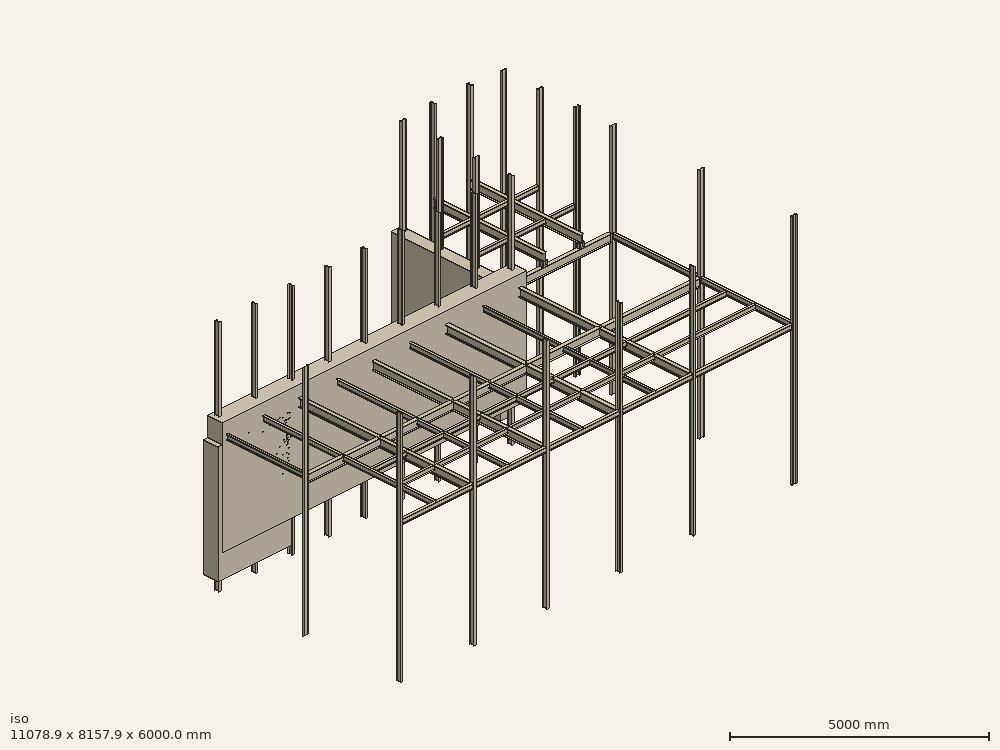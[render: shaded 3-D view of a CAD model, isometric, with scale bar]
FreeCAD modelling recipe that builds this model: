
FCSTD DOCUMENT  (FreeCAD 0.21R33321 (Git))
Label: 20230601-sunroom-layout
License: All rights reserved
LicenseURL: http://en.wikipedia.org/wiki/All_rights_reserved
objects: Part::Part2DObjectPython×96, Part::FeaturePython×55, App::DocumentObjectGroup×13, App::MeasureDistance×1, Spreadsheet::Sheet×1, App::GeometryPython×1
note: 152 computed .brp shape members not serialized (recipe doc carries the construction recipe); baked Part::Feature solids carry a one-line shape summary decoded from their .brp

FEATURE [Part::Part2DObjectPython] Rectangle001  label="Rect-sec1"  # Draft 2D object (typed FeaturePython)
  Area = 800000
  ChamferSize = 0
  Columns = 1
  FilletRadius = 0
  Height = 400
  Length = 2000
  MakeFace = true
  Placement = pos=(-5613.61,2200,0) rot=(0,0,1;0rad)
  Rows = 1
FEATURE [Part::FeaturePython] Wall  label="NorthWall1-400mm"  # Arch/BIM 166 (typed FeaturePython)
  Align = 2
  Area = 0
  Base = -> Rectangle001
  BlockHeight = 0
  BlockLength = 0
  CountBroken = 0
  CountEntire = 0
  Face = 0
  Height = 3000
  HorizontalArea = 800000
  IfcData = attributes={"GlobalId": {"name": "GlobalId", "type": "IfcGloballyUniqueId", "is_enum": false, "enum_values": []}, "Description": {"... (+533 chars omitted),+1 more (map truncated)
  IfcType = 166
  Joint = 0
  Length = 0
  MakeBlocks = false
  MoveBase = false
  MoveWithHost = false
  Normal = (0,0,0)
  OffsetFirst = 0
  OffsetSecond = 0
  PerimeterLength = 4800
  Placement = pos=(0,0,-600) rot=(0,0,1;0rad)
  PredefinedType = 0
  VerticalArea = 1.44e+07
  Width = 200
FEATURE [App::MeasureDistance] Distance  label="Distance: 2363.01 mm"
  Distance = 2398.43
  P1 = (-3738.2,2140,2600)
  P2 = (-3709.77,2140,4998.26)
FEATURE [Spreadsheet::Sheet] Spreadsheet  label="S"
  cells = A1=BaseHeight; B1(BaseHeight)==5200 mm; A2=BaseLength; B2(BaseLength)==11000 mm; A3=BaseSlabThickness; B3(BaseSlabThickness)==200 mm; A4=ColHeight; B4(ColHeight)==6000 mm; A5=NorthWallThickness; B5(NorthWallThickness)==400 mm; A6=SouthWallThickness; B6(SouthWallThickness)==200 mm; A7=LaundryRoomWidth; B7(LaundryRoomWidth)==3 m; A8=LaundryRoomDepth; B8(LaundryRoomDepth)==3 m; A9=col1xpos; B9(col1xpos)==-BaseLength / 2 + 100 mm; A10=col1ypos; B10(col1ypos)==BaseHeight / 2 - NorthWallThickness / 2; A11=col1xposIPE; B11(col1xposIPE)==col1xpos + 32 mm; A12=col1yposIPE; B12(col1yposIPE)==col1ypos + 60 mm; A13=colwidth; B13(colwidth)==64 mm; A14=colheight; B14(collength)==120 mm; A15=vertcoltype; B15(vertcoltype)=IPE120
FEATURE [Part::Part2DObjectPython] Rectangle003  label="NorthWallRect"  # Draft 2D object (typed FeaturePython)
  Area = 3320000
  ChamferSize = 0
  Columns = 1
  FilletRadius = 0
  Height = 400
  Length = 8300
  MakeFace = true
  Placement = pos=(-5500,2200,0) rot=(0,0,1;0rad)
  Rows = 1
  expr: .Placement.Base.x = -Spreadsheet.BaseLength / 2
  expr: .Placement.Base.y = Spreadsheet.BaseHeight / 2 - Spreadsheet.NorthWallThickness
  expr: Height = Spreadsheet.NorthWallThickness
  expr: Length = Spreadsheet.BaseLength - 3 m + 300 mm
FEATURE [Part::Part2DObjectPython] Rectangle004  label="SouthWallRect"  # Draft 2D object (typed FeaturePython)
  Area = 2200000
  ChamferSize = 0
  Columns = 1
  FilletRadius = 0
  Height = 200
  Length = 11000
  MakeFace = true
  Placement = pos=(-5500,-2600,0) rot=(0,0,1;0rad)
  Rows = 1
  expr: .Placement.Base.x = -Spreadsheet.BaseLength / 2
  expr: .Placement.Base.y = -Spreadsheet.BaseHeight / 2
  expr: Height = Spreadsheet.SouthWallThickness
  expr: Length = Spreadsheet.BaseLength
FEATURE [Part::Part2DObjectPython] Rectangle005  label="NorthColPosRect"  # Draft 2D object (typed FeaturePython)
  Area = 960000
  ChamferSize = 0
  Columns = 1
  FilletRadius = 0
  Height = 120
  Length = 8000
  MakeFace = true
  Placement = pos=(-5500,2400,0) rot=(0,0,1;0rad)
  Rows = 1
  expr: .Placement.Base.x = -Spreadsheet.BaseLength / 2
  expr: .Placement.Base.y = Spreadsheet.BaseHeight / 2 - Spreadsheet.NorthWallThickness / 2
FEATURE [Part::Part2DObjectPython] Rectangle006  label="WestWallRect"  # Draft 2D object (typed FeaturePython)
  Area = 920000
  ChamferSize = 0
  Columns = 1
  FilletRadius = 0
  Height = 4600
  Length = 200
  MakeFace = true
  Placement = pos=(-5500,-2400,0) rot=(0,0,1;0rad)
  Rows = 1
  expr: Height = Spreadsheet.BaseHeight - Spreadsheet.NorthWallThickness - Spreadsheet.SouthWallThickness
  expr: Length = Spreadsheet.SouthWallThickness
FEATURE [Part::Part2DObjectPython] Rectangle007  label="Col1Rect"  # Draft 2D object (typed FeaturePython)
  Area = 7680
  ChamferSize = 0
  Columns = 1
  FilletRadius = 0
  Height = 120
  Length = 64
  MakeFace = true
  Placement = pos=(-5400,2400,0) rot=(0,0,1;0rad)
  Rows = 1
  expr: .Placement.Base.x = Spreadsheet.col1xpos
  expr: .Placement.Base.y = Spreadsheet.col1ypos
  expr: Height = Spreadsheet.collength
  expr: Length = Spreadsheet.colwidth
FEATURE [Part::Part2DObjectPython] Clone2D  label="Col2Rect (2D)"  # Draft 2D object (typed FeaturePython)
  Fuse = false
  Objects = -> [Rectangle007]
  Placement = pos=(-4400,2400,0) rot=(0,0,1;0rad)
  Scale = (1,1,1)
  expr: .Placement.Base.x = Spreadsheet.col1xpos + 1000 mm
  expr: .Placement.Base.y = Spreadsheet.col1ypos
FEATURE [Part::Part2DObjectPython] Clone2D001  label="Col3Rect (2D)"  # Draft 2D object (typed FeaturePython)
  Fuse = false
  Objects = -> [Rectangle007]
  Placement = pos=(-3400,2400,0) rot=(0,0,1;0rad)
  Scale = (1,1,1)
  expr: .Placement.Base.x = Spreadsheet.col1xpos + 2000 mm
FEATURE [Part::Part2DObjectPython] Clone2D002  label="Col4Rect (2D)"  # Draft 2D object (typed FeaturePython)
  Fuse = false
  Objects = -> [Rectangle007]
  Placement = pos=(-2400,2400,0) rot=(0,0,1;0rad)
  Scale = (1,1,1)
  expr: .Placement.Base.x = Spreadsheet.col1xpos + 3000 mm
  expr: .Placement.Base.y = Spreadsheet.col1ypos
FEATURE [Part::Part2DObjectPython] Clone2D003  label="Col5Rect (2D)"  # Draft 2D object (typed FeaturePython)
  Fuse = false
  Objects = -> [Rectangle007]
  Placement = pos=(-1400,2400,0) rot=(0,0,1;0rad)
  Scale = (1,1,1)
  expr: .Placement.Base.x = Spreadsheet.col1xpos + 4000 mm
  expr: .Placement.Base.y = Spreadsheet.col1ypos
FEATURE [Part::Part2DObjectPython] Clone2D004  label="Col7Rect (2D)"  # Draft 2D object (typed FeaturePython)
  Fuse = false
  Objects = -> [Rectangle007]
  Placement = pos=(600,2400,0) rot=(0,0,1;0rad)
  Scale = (1,1,1)
  expr: .Placement.Base.x = Spreadsheet.col1xpos + 6000 mm
  expr: .Placement.Base.y = Spreadsheet.col1ypos
FEATURE [Part::Part2DObjectPython] Clone2D005  label="Col6Rect (2D)"  # Draft 2D object (typed FeaturePython)
  Fuse = false
  Objects = -> [Rectangle007]
  Placement = pos=(-400,2400,0) rot=(0,0,1;0rad)
  Scale = (1,1,1)
  expr: .Placement.Base.x = Spreadsheet.col1xpos + 5000 mm
  expr: .Placement.Base.y = Spreadsheet.col1ypos
FEATURE [Part::Part2DObjectPython] Clone2D006  label="Col8Rect (2D)"  # Draft 2D object (typed FeaturePython)
  Fuse = false
  Objects = -> [Rectangle007]
  Placement = pos=(1600,2400,0) rot=(0,0,1;0rad)
  Scale = (1,1,1)
  expr: .Placement.Base.x = Spreadsheet.col1xpos + 7000 mm
  expr: .Placement.Base.y = Spreadsheet.col1ypos
FEATURE [Part::Part2DObjectPython] Rectangle008  label="LaundryRoomRect"  # Draft 2D object (typed FeaturePython)
  Area = 9000000
  ChamferSize = 0
  Columns = 1
  FilletRadius = 0
  Height = 3000
  Length = 3000
  MakeFace = true
  Placement = pos=(2500,2600,0) rot=(0,0,1;0rad)
  Rows = 1
  expr: .Placement.Base.x = 2500
  expr: Height = Spreadsheet.LaundryRoomDepth
  expr: Length = Spreadsheet.LaundryRoomDepth
FEATURE [Part::Part2DObjectPython] Clone2D007  label="Col9Rect (2D)"  # Draft 2D object (typed FeaturePython)
  Fuse = false
  Objects = -> [Rectangle007]
  Placement = pos=(2602.84,2400.21,0) rot=(0,0,1;0rad)
  Scale = (1,1,1)
FEATURE [App::DocumentObjectGroup] Group001  label="RectN"
  Group = -> [Rectangle007,Clone2D,Clone2D001,Clone2D002,Clone2D003,Clone2D005,Clone2D004,Clone2D006,Clone2D007]
FEATURE [Part::Part2DObjectPython] Clone2D008  label="Col10Rect (2D)"  # Draft 2D object (typed FeaturePython)
  Fuse = false
  Objects = -> [Clone2D007]
  Placement = pos=(2720,3400,0) rot=(0,0,1;1.5708rad)
  Scale = (1,1,1)
  expr: .Placement.Base.x = 2720 mm
  expr: .Placement.Base.y = 2400 mm + 1000 mm
FEATURE [Part::Part2DObjectPython] IPE120005  # Draft 2D object (typed FeaturePython)
  FlangeThickness = 6.3
  Height = 120
  WebThickness = 4.4
  Width = 64
FEATURE [Part::FeaturePython] Structure006  label="Col5"  # Arch/BIM 24 (typed FeaturePython)
  Base = -> IPE120005
  BaseMirror = false
  BaseOffsetX = 0
  BaseOffsetY = 0
  BasePerpendicularToTool = false
  BaseRotation = 0
  ComputedLength = 6000
  FaceMaker = 0
  Height = 6000
  HorizontalArea = 1278.96
  IfcData = attributes={"GlobalId": {"name": "GlobalId", "type": "IfcGloballyUniqueId", "is_enum": false, "enum_values": []}, "Description": {"... (+438 chars omitted),+1 more (map truncated)
  IfcType = 24
  Length = 120
  MoveBase = false
  MoveWithHost = false
  Nodes = (2) [(0,-1.61713e-15,0),(0,-1.61713e-15,6000)]
  NodesOffset = 0
  Normal = (0,0,0)
  PerimeterLength = 487.2
  Placement = pos=(-1368,2460,-1000) rot=(0,0,1;0rad)
  PredefinedType = 0
  Profile = IPE120
  ToolOffsetFirst = 0
  ToolOffsetLast = 0
  VerticalArea = 2923200
  Width = 64
  expr: .Placement.Base.x = Spreadsheet.col1xposIPE + 4000 mm
  expr: .Placement.Base.y = Spreadsheet.col1yposIPE
FEATURE [Part::Part2DObjectPython] IPE120006  # Draft 2D object (typed FeaturePython)
  FlangeThickness = 6.3
  Height = 120
  WebThickness = 4.4
  Width = 64
FEATURE [Part::FeaturePython] Structure007  label="Col6"  # Arch/BIM 24 (typed FeaturePython)
  Base = -> IPE120006
  BaseMirror = false
  BaseOffsetX = 0
  BaseOffsetY = 0
  BasePerpendicularToTool = false
  BaseRotation = 0
  ComputedLength = 6000
  FaceMaker = 0
  Height = 6000
  HorizontalArea = 1278.96
  IfcData = attributes={"GlobalId": {"name": "GlobalId", "type": "IfcGloballyUniqueId", "is_enum": false, "enum_values": []}, "Description": {"... (+438 chars omitted),+1 more (map truncated)
  IfcType = 24
  Length = 120
  MoveBase = false
  MoveWithHost = false
  Nodes = (2) [(0,-1.61713e-15,0),(0,-1.61713e-15,6000)]
  NodesOffset = 0
  Normal = (0,0,0)
  PerimeterLength = 487.2
  Placement = pos=(-368,2460,-1000) rot=(0,0,1;0rad)
  PredefinedType = 0
  Profile = IPE120
  ToolOffsetFirst = 0
  ToolOffsetLast = 0
  VerticalArea = 2923200
  Width = 64
  expr: .Placement.Base.x = Spreadsheet.col1xposIPE + 5000 mm
  expr: .Placement.Base.y = Spreadsheet.col1yposIPE
FEATURE [Part::Part2DObjectPython] IPE120007  # Draft 2D object (typed FeaturePython)
  FlangeThickness = 6.3
  Height = 120
  WebThickness = 4.4
  Width = 64
FEATURE [Part::FeaturePython] Structure008  label="Col7"  # Arch/BIM 24 (typed FeaturePython)
  Base = -> IPE120007
  BaseMirror = false
  BaseOffsetX = 0
  BaseOffsetY = 0
  BasePerpendicularToTool = false
  BaseRotation = 0
  ComputedLength = 6000
  FaceMaker = 0
  Height = 6000
  HorizontalArea = 1278.96
  IfcData = attributes={"GlobalId": {"name": "GlobalId", "type": "IfcGloballyUniqueId", "is_enum": false, "enum_values": []}, "Description": {"... (+438 chars omitted),+1 more (map truncated)
  IfcType = 24
  Length = 120
  MoveBase = false
  MoveWithHost = false
  Nodes = (2) [(0,-1.61713e-15,0),(0,-1.61713e-15,6000)]
  NodesOffset = 0
  Normal = (0,0,0)
  PerimeterLength = 487.2
  Placement = pos=(632,2460,-1000) rot=(0,0,1;0rad)
  PredefinedType = 0
  Profile = IPE120
  ToolOffsetFirst = 0
  ToolOffsetLast = 0
  VerticalArea = 2923200
  Width = 64
  expr: .Placement.Base.x = Spreadsheet.col1xposIPE + 6000 mm
  expr: .Placement.Base.y = Spreadsheet.col1yposIPE
FEATURE [Part::Part2DObjectPython] IPE120008  # Draft 2D object (typed FeaturePython)
  FlangeThickness = 6.3
  Height = 120
  WebThickness = 4.4
  Width = 64
FEATURE [Part::FeaturePython] Structure009  label="Col8"  # Arch/BIM 24 (typed FeaturePython)
  Base = -> IPE120008
  BaseMirror = false
  BaseOffsetX = 0
  BaseOffsetY = 0
  BasePerpendicularToTool = false
  BaseRotation = 0
  ComputedLength = 6000
  FaceMaker = 0
  Height = 6000
  HorizontalArea = 1278.96
  IfcData = attributes={"GlobalId": {"name": "GlobalId", "type": "IfcGloballyUniqueId", "is_enum": false, "enum_values": []}, "Description": {"... (+438 chars omitted),+1 more (map truncated)
  IfcType = 24
  Length = 120
  MoveBase = false
  MoveWithHost = false
  Nodes = (2) [(0,-1.61713e-15,0),(0,-1.61713e-15,6000)]
  NodesOffset = 0
  Normal = (0,0,0)
  PerimeterLength = 487.2
  Placement = pos=(1632,2460,-1000) rot=(0,0,1;0rad)
  PredefinedType = 0
  Profile = IPE120
  ToolOffsetFirst = 0
  ToolOffsetLast = 0
  VerticalArea = 2923200
  Width = 64
  expr: .Placement.Base.x = Spreadsheet.col1xposIPE + 7000 mm
  expr: .Placement.Base.y = Spreadsheet.col1yposIPE
FEATURE [Part::Part2DObjectPython] IPE120009  # Draft 2D object (typed FeaturePython)
  FlangeThickness = 6.3
  Height = 120
  WebThickness = 4.4
  Width = 64
FEATURE [Part::FeaturePython] Structure010  label="Col9"  # Arch/BIM 24 (typed FeaturePython)
  Base = -> IPE120009
  BaseMirror = false
  BaseOffsetX = 0
  BaseOffsetY = 0
  BasePerpendicularToTool = false
  BaseRotation = 0
  ComputedLength = 6000
  FaceMaker = 0
  Height = 6000
  HorizontalArea = 1278.96
  IfcData = attributes={"GlobalId": {"name": "GlobalId", "type": "IfcGloballyUniqueId", "is_enum": false, "enum_values": []}, "Description": {"... (+438 chars omitted),+1 more (map truncated)
  IfcType = 24
  Length = 120
  MoveBase = false
  MoveWithHost = false
  Nodes = (2) [(0,-1.61713e-15,0),(0,-1.61713e-15,6000)]
  NodesOffset = 0
  Normal = (0,0,0)
  PerimeterLength = 487.2
  Placement = pos=(2634.76,2460.15,-1000) rot=(0,0,1;0rad)
  PredefinedType = 0
  Profile = IPE120
  ToolOffsetFirst = 0
  ToolOffsetLast = 0
  VerticalArea = 2923200
  Width = 64
FEATURE [Part::Part2DObjectPython] Rectangle009  label="LaundryWallWestRect"  # Draft 2D object (typed FeaturePython)
  Area = 900000
  ChamferSize = 0
  Columns = 1
  FilletRadius = 0
  Height = 3000
  Length = 300
  MakeFace = true
  Placement = pos=(2500.39,2600,0) rot=(0,0,1;0rad)
  Rows = 1
  expr: Height = Spreadsheet.LaundryRoomDepth
FEATURE [Part::Part2DObjectPython] Clone2D009  label="Col11Rect (2D)"  # Draft 2D object (typed FeaturePython)
  Fuse = false
  Objects = -> [Clone2D008]
  Placement = pos=(2720,4400,0) rot=(0,0,1;1.5708rad)
  Scale = (1,1,1)
  expr: .Placement.Base.y = 2400 mm + 2000 mm
FEATURE [Part::Part2DObjectPython] Clone2D010  label="Col12Rect (2D)"  # Draft 2D object (typed FeaturePython)
  Fuse = false
  Objects = -> [Clone2D009]
  Placement = pos=(2720,5400,0) rot=(0,0,1;1.5708rad)
  Scale = (1,1,1)
  expr: .Placement.Base.y = 2400 mm + 3000 mm
FEATURE [Part::Part2DObjectPython] Rectangle010  label="LaundryWallEastRect"  # Draft 2D object (typed FeaturePython)
  Area = 600000
  ChamferSize = 0
  Columns = 1
  FilletRadius = 0
  Height = 3000
  Length = 200
  MakeFace = true
  Placement = pos=(5300,2600,0) rot=(0,0,1;0rad)
  Rows = 1
  expr: Height = Spreadsheet.LaundryRoomDepth
FEATURE [Part::Part2DObjectPython] Clone2D011  label="Col15Rect (2D)"  # Draft 2D object (typed FeaturePython)
  Fuse = false
  Objects = -> [Clone2D010]
  Placement = pos=(5465.32,5400,0) rot=(0,0,1;1.5708rad)
  Scale = (1,1,1)
FEATURE [Part::Part2DObjectPython] Clone2D012  label="Col16Rect (2D)"  # Draft 2D object (typed FeaturePython)
  Fuse = false
  Objects = -> [Clone2D009]
  Placement = pos=(5465.32,4400,0) rot=(0,0,1;1.5708rad)
  Scale = (1,1,1)
FEATURE [Part::Part2DObjectPython] Clone2D013  label="Col17Rect (2D)"  # Draft 2D object (typed FeaturePython)
  Fuse = false
  Objects = -> [Clone2D008]
  Placement = pos=(5465.32,3400,0) rot=(0,0,1;1.5708rad)
  Scale = (1,1,1)
FEATURE [Part::Part2DObjectPython] Clone2D014  label="Col14Rect (2D)"  # Draft 2D object (typed FeaturePython)
  Fuse = false
  Objects = -> [Clone2D006]
  Placement = pos=(4509.76,5428.53,0) rot=(0,0,1;0rad)
  Scale = (1,1,1)
FEATURE [Part::Part2DObjectPython] Clone2D015  label="Col13Rect (2D)"  # Draft 2D object (typed FeaturePython)
  Fuse = false
  Objects = -> [Clone2D004]
  Placement = pos=(3509.76,5428.53,0) rot=(0,0,1;0rad)
  Scale = (1,1,1)
FEATURE [App::DocumentObjectGroup] Group004  label="Rect"
  Group = -> [Clone2D010,Clone2D009,Clone2D008,Clone2D011,Clone2D012,Clone2D013,Clone2D014,Clone2D015]
FEATURE [Part::Part2DObjectPython] Rectangle011  label="EastWallRect"  # Draft 2D object (typed FeaturePython)
  Area = 1000000
  ChamferSize = 0
  Columns = 1
  FilletRadius = 0
  Height = 5000
  Length = 200
  MakeFace = true
  Placement = pos=(5300,-2400,0) rot=(0,0,1;0rad)
  Rows = 1
FEATURE [App::GeometryPython] BuildingPart  label="Floor"  # Arch/BIM 14 (typed FeaturePython)
  Area = 0
  CompositionType = 0
  Elevation = 0
  Group = -> [Rectangle005,Rectangle011,Rectangle004,Rectangle008,Rectangle009,Rectangle010,Rectangle006]
  Height = 0
  HeightPropagate = true
  IfcData = attributes={"GlobalId": {"name": "GlobalId", "type": "IfcGloballyUniqueId", "is_enum": false, "enum_values": []}, "Description": {"... (+866 chars omitted),+1 more (map truncated)
  IfcType = 14
  LevelOffset = 0
  LongName = Floor
  OnlySolids = true
  expr: Elevation = .Placement.Base.z
FEATURE [Part::Part2DObjectPython] Clone2D016  label="Col18Rect (2D)"  # Draft 2D object (typed FeaturePython)
  Fuse = false
  Objects = -> [Clone2D007]
  Placement = pos=(5460,2400,0) rot=(0,0,1;1.5708rad)
  Scale = (1,1,1)
FEATURE [Part::Part2DObjectPython] IPE120011  # Draft 2D object (typed FeaturePython)
  FlangeThickness = 6.3
  Height = 120
  WebThickness = 4.4
  Width = 64
FEATURE [Part::FeaturePython] Structure011  label="Col13"  # Arch/BIM 24 (typed FeaturePython)
  Base = -> IPE120011
  BaseMirror = false
  BaseOffsetX = 0
  BaseOffsetY = 0
  BasePerpendicularToTool = false
  BaseRotation = 0
  ComputedLength = 6000
  FaceMaker = 0
  Height = 6000
  HorizontalArea = 1278.96
  IfcData = attributes={"GlobalId": {"name": "GlobalId", "type": "IfcGloballyUniqueId", "is_enum": false, "enum_values": []}, "Description": {"... (+438 chars omitted),+1 more (map truncated)
  IfcType = 24
  Length = 120
  MoveBase = false
  MoveWithHost = false
  Nodes = (2) [(0,-1.61713e-15,0),(0,-1.61713e-15,6000)]
  NodesOffset = 0
  Normal = (0,0,0)
  PerimeterLength = 487.2
  Placement = pos=(3541.76,5488.53,-1000) rot=(0,0,-1;0rad)
  PredefinedType = 0
  Profile = IPE120
  ToolOffsetFirst = 0
  ToolOffsetLast = 0
  VerticalArea = 2923200
  Width = 64
FEATURE [Part::Part2DObjectPython] IPE120012  # Draft 2D object (typed FeaturePython)
  FlangeThickness = 6.3
  Height = 120
  WebThickness = 4.4
  Width = 64
FEATURE [Part::FeaturePython] Structure012  label="Col14"  # Arch/BIM 24 (typed FeaturePython)
  Base = -> IPE120012
  BaseMirror = false
  BaseOffsetX = 0
  BaseOffsetY = 0
  BasePerpendicularToTool = false
  BaseRotation = 0
  ComputedLength = 6000
  FaceMaker = 0
  Height = 6000
  HorizontalArea = 1278.96
  IfcData = attributes={"GlobalId": {"name": "GlobalId", "type": "IfcGloballyUniqueId", "is_enum": false, "enum_values": []}, "Description": {"... (+438 chars omitted),+1 more (map truncated)
  IfcType = 24
  Length = 120
  MoveBase = false
  MoveWithHost = false
  Nodes = (2) [(0,-1.61713e-15,0),(0,-1.61713e-15,6000)]
  NodesOffset = 0
  Normal = (0,0,0)
  PerimeterLength = 487.2
  Placement = pos=(4541.76,5488.53,-1000) rot=(0,0,1;0rad)
  PredefinedType = 0
  Profile = IPE120
  ToolOffsetFirst = 0
  ToolOffsetLast = 0
  VerticalArea = 2923200
  Width = 64
FEATURE [Part::Part2DObjectPython] IPE120013  # Draft 2D object (typed FeaturePython)
  FlangeThickness = 6.3
  Height = 120
  WebThickness = 4.4
  Width = 64
FEATURE [Part::FeaturePython] Structure013  label="Col12"  # Arch/BIM 24 (typed FeaturePython)
  Base = -> IPE120013
  BaseMirror = false
  BaseOffsetX = 0
  BaseOffsetY = 0
  BasePerpendicularToTool = false
  BaseRotation = 0
  ComputedLength = 6000
  FaceMaker = 0
  Height = 6000
  HorizontalArea = 1278.96
  IfcData = attributes={"GlobalId": {"name": "GlobalId", "type": "IfcGloballyUniqueId", "is_enum": false, "enum_values": []}, "Description": {"... (+438 chars omitted),+1 more (map truncated)
  IfcType = 24
  Length = 120
  MoveBase = false
  MoveWithHost = false
  Nodes = (2) [(0,-1.61713e-15,0),(0,-1.61713e-15,6000)]
  NodesOffset = 0
  Normal = (0,0,0)
  PerimeterLength = 487.2
  Placement = pos=(2660,5432,-1000) rot=(0,0,1;1.5708rad)
  PredefinedType = 0
  Profile = IPE120
  ToolOffsetFirst = 0
  ToolOffsetLast = 0
  VerticalArea = 2923200
  Width = 64
FEATURE [Part::Part2DObjectPython] IPE120014  # Draft 2D object (typed FeaturePython)
  FlangeThickness = 6.3
  Height = 120
  WebThickness = 4.4
  Width = 64
FEATURE [Part::FeaturePython] Structure014  label="Col11"  # Arch/BIM 24 (typed FeaturePython)
  Base = -> IPE120014
  BaseMirror = false
  BaseOffsetX = 0
  BaseOffsetY = 0
  BasePerpendicularToTool = false
  BaseRotation = 0
  ComputedLength = 6000
  FaceMaker = 0
  Height = 6000
  HorizontalArea = 1278.96
  IfcData = attributes={"GlobalId": {"name": "GlobalId", "type": "IfcGloballyUniqueId", "is_enum": false, "enum_values": []}, "Description": {"... (+438 chars omitted),+1 more (map truncated)
  IfcType = 24
  Length = 120
  MoveBase = false
  MoveWithHost = false
  Nodes = (2) [(0,-1.61713e-15,0),(0,-1.61713e-15,6000)]
  NodesOffset = 0
  Normal = (0,0,0)
  PerimeterLength = 487.2
  Placement = pos=(2660,4432,-1000) rot=(0,0,1;1.5708rad)
  PredefinedType = 0
  Profile = IPE120
  ToolOffsetFirst = 0
  ToolOffsetLast = 0
  VerticalArea = 2923200
  Width = 64
FEATURE [Part::Part2DObjectPython] IPE120015  # Draft 2D object (typed FeaturePython)
  FlangeThickness = 6.3
  Height = 120
  WebThickness = 4.4
  Width = 64
FEATURE [Part::FeaturePython] Structure015  label="Col10"  # Arch/BIM 24 (typed FeaturePython)
  Base = -> IPE120015
  BaseMirror = false
  BaseOffsetX = 0
  BaseOffsetY = 0
  BasePerpendicularToTool = false
  BaseRotation = 0
  ComputedLength = 6000
  FaceMaker = 0
  Height = 6000
  HorizontalArea = 1278.96
  IfcData = attributes={"GlobalId": {"name": "GlobalId", "type": "IfcGloballyUniqueId", "is_enum": false, "enum_values": []}, "Description": {"... (+438 chars omitted),+1 more (map truncated)
  IfcType = 24
  Length = 120
  MoveBase = false
  MoveWithHost = false
  Nodes = (2) [(0,-1.61713e-15,0),(0,-1.61713e-15,6000)]
  NodesOffset = 0
  Normal = (0,0,0)
  PerimeterLength = 487.2
  Placement = pos=(2660,3432,-1000) rot=(0,0,1;1.5708rad)
  PredefinedType = 0
  Profile = IPE120
  ToolOffsetFirst = 0
  ToolOffsetLast = 0
  VerticalArea = 2923200
  Width = 64
FEATURE [Part::Part2DObjectPython] IPE120016  # Draft 2D object (typed FeaturePython)
  FlangeThickness = 6.3
  Height = 120
  WebThickness = 4.4
  Width = 64
FEATURE [Part::FeaturePython] Structure016  label="Col15"  # Arch/BIM 24 (typed FeaturePython)
  Base = -> IPE120016
  BaseMirror = false
  BaseOffsetX = 0
  BaseOffsetY = 0
  BasePerpendicularToTool = false
  BaseRotation = 0
  ComputedLength = 6000
  FaceMaker = 0
  Height = 6000
  HorizontalArea = 1278.96
  IfcData = attributes={"GlobalId": {"name": "GlobalId", "type": "IfcGloballyUniqueId", "is_enum": false, "enum_values": []}, "Description": {"... (+438 chars omitted),+1 more (map truncated)
  IfcType = 24
  Length = 120
  MoveBase = false
  MoveWithHost = false
  Nodes = (2) [(0,-1.61713e-15,0),(0,-1.61713e-15,6000)]
  NodesOffset = 0
  Normal = (0,0,0)
  PerimeterLength = 487.2
  Placement = pos=(5405.32,5432,-1000) rot=(0,0,1;1.5708rad)
  PredefinedType = 0
  Profile = IPE120
  ToolOffsetFirst = 0
  ToolOffsetLast = 0
  VerticalArea = 2923200
  Width = 64
FEATURE [Part::Part2DObjectPython] IPE120017  # Draft 2D object (typed FeaturePython)
  FlangeThickness = 6.3
  Height = 120
  WebThickness = 4.4
  Width = 64
FEATURE [Part::FeaturePython] Structure017  label="Col16"  # Arch/BIM 24 (typed FeaturePython)
  Base = -> IPE120017
  BaseMirror = false
  BaseOffsetX = 0
  BaseOffsetY = 0
  BasePerpendicularToTool = false
  BaseRotation = 0
  ComputedLength = 6000
  FaceMaker = 0
  Height = 6000
  HorizontalArea = 1278.96
  IfcData = attributes={"GlobalId": {"name": "GlobalId", "type": "IfcGloballyUniqueId", "is_enum": false, "enum_values": []}, "Description": {"... (+438 chars omitted),+1 more (map truncated)
  IfcType = 24
  Length = 120
  MoveBase = false
  MoveWithHost = false
  Nodes = (2) [(0,-1.61713e-15,0),(0,-1.61713e-15,6000)]
  NodesOffset = 0
  Normal = (0,0,0)
  PerimeterLength = 487.2
  Placement = pos=(5405.27,4431.98,-1000) rot=(0,0,1;1.5708rad)
  PredefinedType = 0
  Profile = IPE120
  ToolOffsetFirst = 0
  ToolOffsetLast = 0
  VerticalArea = 2923200
  Width = 64
FEATURE [Part::Part2DObjectPython] IPE120018  # Draft 2D object (typed FeaturePython)
  FlangeThickness = 6.3
  Height = 120
  WebThickness = 4.4
  Width = 64
FEATURE [Part::FeaturePython] Structure018  label="Col17"  # Arch/BIM 24 (typed FeaturePython)
  Base = -> IPE120018
  BaseMirror = false
  BaseOffsetX = 0
  BaseOffsetY = 0
  BasePerpendicularToTool = false
  BaseRotation = 0
  ComputedLength = 6000
  FaceMaker = 0
  Height = 6000
  HorizontalArea = 1278.96
  IfcData = attributes={"GlobalId": {"name": "GlobalId", "type": "IfcGloballyUniqueId", "is_enum": false, "enum_values": []}, "Description": {"... (+438 chars omitted),+1 more (map truncated)
  IfcType = 24
  Length = 120
  MoveBase = false
  MoveWithHost = false
  Nodes = (2) [(0,-1.61713e-15,0),(0,-1.61713e-15,6000)]
  NodesOffset = 0
  Normal = (0,0,0)
  PerimeterLength = 487.2
  Placement = pos=(5405.32,3432,-1000) rot=(0,0,1;1.5708rad)
  PredefinedType = 0
  Profile = IPE120
  ToolOffsetFirst = 0
  ToolOffsetLast = 0
  VerticalArea = 2923200
  Width = 64
FEATURE [Part::Part2DObjectPython] Rectangle012  label="LaundryWallNorth"  # Draft 2D object (typed FeaturePython)
  Area = 750000
  ChamferSize = 0
  Columns = 1
  FilletRadius = 0
  Height = 300
  Length = 2500
  MakeFace = true
  Placement = pos=(2800,5300,0) rot=(0,0,1;0rad)
  Rows = 1
FEATURE [Part::Part2DObjectPython] Rectangle013  label="LaundryFloorSlabRect"  # Draft 2D object (typed FeaturePython)
  Area = 6750000
  ChamferSize = 0
  Columns = 1
  FilletRadius = 0
  Height = 2700
  Length = 2500
  MakeFace = true
  Placement = pos=(2802.36,2601.58,0) rot=(0,0,1;0rad)
  Rows = 1
FEATURE [Part::Part2DObjectPython] IPE120019  # Draft 2D object (typed FeaturePython)
  FlangeThickness = 6.3
  Height = 120
  WebThickness = 4.4
  Width = 64
FEATURE [Part::FeaturePython] Structure019  label="Col18"  # Arch/BIM 24 (typed FeaturePython)
  Base = -> IPE120019
  BaseMirror = false
  BaseOffsetX = 0
  BaseOffsetY = 0
  BasePerpendicularToTool = false
  BaseRotation = 0
  ComputedLength = 6000
  FaceMaker = 0
  Height = 6000
  HorizontalArea = 1278.96
  IfcData = attributes={"GlobalId": {"name": "GlobalId", "type": "IfcGloballyUniqueId", "is_enum": false, "enum_values": []}, "Description": {"... (+438 chars omitted),+1 more (map truncated)
  IfcType = 24
  Length = 120
  MoveBase = false
  MoveWithHost = false
  Nodes = (2) [(0,-1.61713e-15,0),(0,-1.61713e-15,6000)]
  NodesOffset = 0
  Normal = (0,0,0)
  PerimeterLength = 487.2
  Placement = pos=(5400,2432,-1000) rot=(0,0,1;1.5708rad)
  PredefinedType = 0
  Profile = IPE120
  ToolOffsetFirst = 0
  ToolOffsetLast = 0
  VerticalArea = 2923200
  Width = 64
FEATURE [Part::Part2DObjectPython] Clone2D017  label="Col31Rect"  # Draft 2D object (typed FeaturePython)
  Fuse = false
  Objects = -> [Rectangle007]
  Placement = pos=(-5400,-2557.73,0) rot=(0,0,1;0rad)
  Scale = (1,1,1)
  expr: .Placement.Base.x = Spreadsheet.col1xpos
FEATURE [Part::Part2DObjectPython] Clone2D018  label="Col30Rect"  # Draft 2D object (typed FeaturePython)
  Fuse = false
  Objects = -> [Clone2D]
  Placement = pos=(-4400,-2557.73,0) rot=(0,0,1;0rad)
  Scale = (1,1,1)
  expr: .Placement.Base.x = Spreadsheet.col1xpos + 1000 mm
FEATURE [Part::Part2DObjectPython] Clone2D019  label="Col29Rect"  # Draft 2D object (typed FeaturePython)
  Fuse = false
  Objects = -> [Clone2D001]
  Placement = pos=(-3400,-2557.73,0) rot=(0,0,1;0rad)
  Scale = (1,1,1)
  expr: .Placement.Base.x = Spreadsheet.col1xpos + 2000 mm
FEATURE [Part::Part2DObjectPython] Clone2D020  label="Col28Rect"  # Draft 2D object (typed FeaturePython)
  Fuse = false
  Objects = -> [Clone2D002]
  Placement = pos=(-2400,-2557.73,0) rot=(0,0,1;0rad)
  Scale = (1,1,1)
  expr: .Placement.Base.x = Spreadsheet.col1xpos + 3000 mm
FEATURE [Part::Part2DObjectPython] Clone2D021  label="Col27Rect"  # Draft 2D object (typed FeaturePython)
  Fuse = false
  Objects = -> [Clone2D003]
  Placement = pos=(-1400,-2557.73,0) rot=(0,0,1;0rad)
  Scale = (1,1,1)
  expr: .Placement.Base.x = Spreadsheet.col1xpos + 4000 mm
FEATURE [Part::Part2DObjectPython] Clone2D022  label="Col26Rect"  # Draft 2D object (typed FeaturePython)
  Fuse = false
  Objects = -> [Clone2D005]
  Placement = pos=(-400,-2557.73,0) rot=(0,0,1;0rad)
  Scale = (1,1,1)
  expr: .Placement.Base.x = Spreadsheet.col1xpos + 5000 mm
FEATURE [Part::Part2DObjectPython] Clone2D023  label="Col25Rect"  # Draft 2D object (typed FeaturePython)
  Fuse = false
  Objects = -> [Clone2D004]
  Placement = pos=(570.338,-2557.73,0) rot=(0,0,1;0rad)
  Scale = (1,1,1)
FEATURE [Part::Part2DObjectPython] Clone2D025  label="Col24Rect"  # Draft 2D object (typed FeaturePython)
  Fuse = false
  Objects = -> [Clone2D020]
  Placement = pos=(1599.92,-2557.73,0) rot=(0,0,1;0rad)
  Scale = (1,1,1)
FEATURE [Part::Part2DObjectPython] Clone2D026  label="Col23Rect"  # Draft 2D object (typed FeaturePython)
  Fuse = false
  Objects = -> [Clone2D021]
  Placement = pos=(2599.92,-2557.73,0) rot=(0,0,1;0rad)
  Scale = (1,1,1)
FEATURE [Part::Part2DObjectPython] Clone2D027  label="Col22Rect"  # Draft 2D object (typed FeaturePython)
  Fuse = false
  Objects = -> [Clone2D022]
  Placement = pos=(3599.92,-2557.73,0) rot=(0,0,1;0rad)
  Scale = (1,1,1)
FEATURE [Part::Part2DObjectPython] Clone2D028  label="Col21Rect"  # Draft 2D object (typed FeaturePython)
  Fuse = false
  Objects = -> [Clone2D023]
  Placement = pos=(4570.26,-2557.73,0) rot=(0,0,1;0rad)
  Scale = (1,1,1)
FEATURE [Part::Part2DObjectPython] Clone2D029  label="Col20Rect"  # Draft 2D object (typed FeaturePython)
  Fuse = false
  Placement = pos=(5460.05,-2532.3,0) rot=(0,0,1;1.5708rad)
  Scale = (1,1,1)
FEATURE [Part::Part2DObjectPython] Clone2D030  label="Col19Rect"  # Draft 2D object (typed FeaturePython)
  Fuse = false
  Objects = -> [Clone2D016]
  Placement = pos=(5460,0,0) rot=(0,0,1;1.5708rad)
  Scale = (1,1,1)
FEATURE [Part::Part2DObjectPython] Clone2D031  label="Col32Rect"  # Draft 2D object (typed FeaturePython)
  Fuse = false
  Objects = -> [Clone2D030]
  Placement = pos=(-5340,0,0) rot=(0,0,1;1.5708rad)
  Scale = (1,1,1)
FEATURE [App::DocumentObjectGroup] Group008  label="RectS"
  Group = -> [Clone2D017,Clone2D018,Clone2D019,Clone2D020,Clone2D021,Clone2D022,Clone2D023,Clone2D025,Clone2D026,Clone2D027,Clone2D028,Clone2D031]
FEATURE [App::DocumentObjectGroup] Group002  label="South"
  Group = -> [Group008]
FEATURE [Part::Part2DObjectPython] IPE120020  # Draft 2D object (typed FeaturePython)
  FlangeThickness = 6.3
  Height = 120
  WebThickness = 4.4
  Width = 64
FEATURE [Part::FeaturePython] Structure020  label="Col29"  # Arch/BIM 24 (typed FeaturePython)
  Base = -> IPE120020
  BaseMirror = false
  BaseOffsetX = 0
  BaseOffsetY = 0
  BasePerpendicularToTool = false
  BaseRotation = 0
  ComputedLength = 6000
  FaceMaker = 0
  Height = 6000
  HorizontalArea = 1278.96
  IfcData = attributes={"GlobalId": {"name": "GlobalId", "type": "IfcGloballyUniqueId", "is_enum": false, "enum_values": []}, "Description": {"... (+438 chars omitted),+1 more (map truncated)
  IfcType = 24
  Length = 120
  MoveBase = false
  MoveWithHost = false
  Nodes = (2) [(0,-1.61713e-15,0),(0,-1.61713e-15,6000)]
  NodesOffset = 0
  Normal = (0,0,0)
  PerimeterLength = 487.2
  Placement = pos=(-3368,-2497.73,-1000) rot=(0,0,1;0rad)
  PredefinedType = 0
  Profile = IPE120
  ToolOffsetFirst = 0
  ToolOffsetLast = 0
  VerticalArea = 2923200
  Width = 64
FEATURE [Part::Part2DObjectPython] IPE120021  # Draft 2D object (typed FeaturePython)
  FlangeThickness = 6.3
  Height = 120
  WebThickness = 4.4
  Width = 64
FEATURE [Part::FeaturePython] Structure021  label="Col27"  # Arch/BIM 24 (typed FeaturePython)
  Base = -> IPE120021
  BaseMirror = false
  BaseOffsetX = 0
  BaseOffsetY = 0
  BasePerpendicularToTool = false
  BaseRotation = 0
  ComputedLength = 6000
  FaceMaker = 0
  Height = 6000
  HorizontalArea = 1278.96
  IfcData = attributes={"GlobalId": {"name": "GlobalId", "type": "IfcGloballyUniqueId", "is_enum": false, "enum_values": []}, "Description": {"... (+438 chars omitted),+1 more (map truncated)
  IfcType = 24
  Length = 120
  MoveBase = false
  MoveWithHost = false
  Nodes = (2) [(0,-1.61713e-15,0),(0,-1.61713e-15,6000)]
  NodesOffset = 0
  Normal = (0,0,0)
  PerimeterLength = 487.2
  Placement = pos=(-1368,-2497.65,-1000) rot=(0,0,1;0rad)
  PredefinedType = 0
  Profile = IPE120
  ToolOffsetFirst = 0
  ToolOffsetLast = 0
  VerticalArea = 2923200
  Width = 64
FEATURE [Part::Part2DObjectPython] IPE120022  # Draft 2D object (typed FeaturePython)
  FlangeThickness = 6.3
  Height = 120
  WebThickness = 4.4
  Width = 64
FEATURE [Part::FeaturePython] Structure022  label="Col25"  # Arch/BIM 24 (typed FeaturePython)
  Base = -> IPE120022
  BaseMirror = false
  BaseOffsetX = 0
  BaseOffsetY = 0
  BasePerpendicularToTool = false
  BaseRotation = 0
  ComputedLength = 6000
  FaceMaker = 0
  Height = 6000
  HorizontalArea = 1278.96
  IfcData = attributes={"GlobalId": {"name": "GlobalId", "type": "IfcGloballyUniqueId", "is_enum": false, "enum_values": []}, "Description": {"... (+438 chars omitted),+1 more (map truncated)
  IfcType = 24
  Length = 120
  MoveBase = false
  MoveWithHost = false
  Nodes = (2) [(0,-1.61713e-15,0),(0,-1.61713e-15,6000)]
  NodesOffset = 0
  Normal = (0,0,0)
  PerimeterLength = 487.2
  Placement = pos=(630.27,-2497.92,-1000) rot=(0,0,1;0rad)
  PredefinedType = 0
  Profile = IPE120
  ToolOffsetFirst = 0
  ToolOffsetLast = 0
  VerticalArea = 2923200
  Width = 64
FEATURE [Part::Part2DObjectPython] IPE120023  # Draft 2D object (typed FeaturePython)
  FlangeThickness = 6.3
  Height = 120
  WebThickness = 4.4
  Width = 64
FEATURE [Part::FeaturePython] Structure023  label="Col23"  # Arch/BIM 24 (typed FeaturePython)
  Base = -> IPE120023
  BaseMirror = false
  BaseOffsetX = 0
  BaseOffsetY = 0
  BasePerpendicularToTool = false
  BaseRotation = 0
  ComputedLength = 6000
  FaceMaker = 0
  Height = 6000
  HorizontalArea = 1278.96
  IfcData = attributes={"GlobalId": {"name": "GlobalId", "type": "IfcGloballyUniqueId", "is_enum": false, "enum_values": []}, "Description": {"... (+438 chars omitted),+1 more (map truncated)
  IfcType = 24
  Length = 120
  MoveBase = false
  MoveWithHost = false
  Nodes = (2) [(0,-1.61713e-15,0),(0,-1.61713e-15,6000)]
  NodesOffset = 0
  Normal = (0,0,0)
  PerimeterLength = 487.2
  Placement = pos=(2631.92,-2497.73,-1000) rot=(0,0,1;0rad)
  PredefinedType = 0
  Profile = IPE120
  ToolOffsetFirst = 0
  ToolOffsetLast = 0
  VerticalArea = 2923200
  Width = 64
FEATURE [Part::Part2DObjectPython] IPE120024  # Draft 2D object (typed FeaturePython)
  FlangeThickness = 6.3
  Height = 120
  WebThickness = 4.4
  Width = 64
FEATURE [Part::FeaturePython] Structure024  label="Col19"  # Arch/BIM 24 (typed FeaturePython)
  Base = -> IPE120024
  BaseMirror = false
  BaseOffsetX = 0
  BaseOffsetY = 0
  BasePerpendicularToTool = false
  BaseRotation = 0
  ComputedLength = 6000
  FaceMaker = 0
  Height = 6000
  HorizontalArea = 1278.96
  IfcData = attributes={"GlobalId": {"name": "GlobalId", "type": "IfcGloballyUniqueId", "is_enum": false, "enum_values": []}, "Description": {"... (+438 chars omitted),+1 more (map truncated)
  IfcType = 24
  Length = 120
  MoveBase = false
  MoveWithHost = false
  Nodes = (2) [(0,-1.61713e-15,0),(0,-1.61713e-15,6000)]
  NodesOffset = 0
  Normal = (0,0,0)
  PerimeterLength = 487.2
  Placement = pos=(5400,32,-1000) rot=(0,0,1;1.5708rad)
  PredefinedType = 0
  Profile = IPE120
  ToolOffsetFirst = 0
  ToolOffsetLast = 0
  VerticalArea = 2923200
  Width = 64
FEATURE [App::DocumentObjectGroup] Group011  label="RectE"
  Group = -> [Clone2D029,Clone2D030]
FEATURE [Part::Part2DObjectPython] IPE120025  # Draft 2D object (typed FeaturePython)
  FlangeThickness = 6.3
  Height = 120
  WebThickness = 4.4
  Width = 64
FEATURE [Part::FeaturePython] Structure025  label="Col31"  # Arch/BIM 24 (typed FeaturePython)
  Base = -> IPE120025
  BaseMirror = false
  BaseOffsetX = 0
  BaseOffsetY = 0
  BasePerpendicularToTool = false
  BaseRotation = 0
  ComputedLength = 6000
  FaceMaker = 0
  Height = 6000
  HorizontalArea = 1278.96
  IfcData = attributes={"GlobalId": {"name": "GlobalId", "type": "IfcGloballyUniqueId", "is_enum": false, "enum_values": []}, "Description": {"... (+438 chars omitted),+1 more (map truncated)
  IfcType = 24
  Length = 120
  MoveBase = false
  MoveWithHost = false
  Nodes = (2) [(0,-1.61713e-15,0),(0,-1.61713e-15,6000)]
  NodesOffset = 0
  Normal = (0,0,0)
  PerimeterLength = 487.2
  Placement = pos=(-5368,-2497.73,-1000) rot=(0,0,1;0rad)
  PredefinedType = 0
  Profile = IPE120
  ToolOffsetFirst = 0
  ToolOffsetLast = 0
  VerticalArea = 2923200
  Width = 64
FEATURE [Part::Part2DObjectPython] IPE120026  # Draft 2D object (typed FeaturePython)
  FlangeThickness = 6.3
  Height = 120
  WebThickness = 4.4
  Width = 64
FEATURE [Part::FeaturePython] Structure026  label="Col32"  # Arch/BIM 24 (typed FeaturePython)
  Base = -> IPE120026
  BaseMirror = false
  BaseOffsetX = 0
  BaseOffsetY = 0
  BasePerpendicularToTool = false
  BaseRotation = 0
  ComputedLength = 6000
  FaceMaker = 0
  Height = 6000
  HorizontalArea = 1278.96
  IfcData = attributes={"GlobalId": {"name": "GlobalId", "type": "IfcGloballyUniqueId", "is_enum": false, "enum_values": []}, "Description": {"... (+438 chars omitted),+1 more (map truncated)
  IfcType = 24
  Length = 120
  MoveBase = false
  MoveWithHost = false
  Nodes = (2) [(0,-1.61713e-15,0),(0,-1.61713e-15,6000)]
  NodesOffset = 0
  Normal = (0,0,0)
  PerimeterLength = 487.2
  Placement = pos=(-5400,32,-1000) rot=(0,0,1;1.5708rad)
  PredefinedType = 0
  Profile = IPE120
  ToolOffsetFirst = 0
  ToolOffsetLast = 0
  VerticalArea = 2923200
  Width = 64
FEATURE [Part::Part2DObjectPython] IPE120028  # Draft 2D object (typed FeaturePython)
  FlangeThickness = 8.5
  Height = 200
  WebThickness = 5.6
  Width = 100
FEATURE [Part::FeaturePython] Structure028  label="Beam2-IPE200"  # Arch/BIM 7 (typed FeaturePython)
  Base = -> IPE120028
  BaseMirror = false
  BaseOffsetX = 0
  BaseOffsetY = 0
  BasePerpendicularToTool = false
  BaseRotation = 0
  ComputedLength = 4838
  FaceMaker = 0
  Height = 4838
  HorizontalArea = 940507
  IfcData = attributes={"GlobalId": {"name": "GlobalId", "type": "IfcGloballyUniqueId", "is_enum": false, "enum_values": []}, "Description": {"... (+475 chars omitted),+1 more (map truncated)
  IfcType = 7
  Length = 200
  MoveBase = false
  MoveWithHost = false
  Nodes = (2) [(0,-1.95917e-14,0),(0,-1.95917e-14,4838)]
  NodesOffset = 0
  Normal = (0,0,0)
  PerimeterLength = 0
  Placement = pos=(-1368.82,2400.24,2500) rot=(1,0,0;1.5708rad)
  PredefinedType = 0
  Profile = IPE200
  ToolOffsetFirst = 0
  ToolOffsetLast = 0
  VerticalArea = 1.94065e+06
  Width = 100
FEATURE [Part::Part2DObjectPython] IPE120029  # Draft 2D object (typed FeaturePython)
  FlangeThickness = 8.5
  Height = 200
  WebThickness = 5.6
  Width = 100
FEATURE [Part::FeaturePython] Structure029  label="Beam4-IPE200"  # Arch/BIM 7 (typed FeaturePython)
  Base = -> IPE120029
  BaseMirror = false
  BaseOffsetX = 0
  BaseOffsetY = 0
  BasePerpendicularToTool = false
  BaseRotation = 0
  ComputedLength = 4838
  FaceMaker = 0
  Height = 4838
  HorizontalArea = 940507
  IfcData = attributes={"GlobalId": {"name": "GlobalId", "type": "IfcGloballyUniqueId", "is_enum": false, "enum_values": []}, "Description": {"... (+475 chars omitted),+1 more (map truncated)
  IfcType = 7
  Length = 200
  MoveBase = false
  MoveWithHost = false
  Nodes = (2) [(0,-1.95917e-14,0),(0,-1.95917e-14,4838)]
  NodesOffset = 0
  Normal = (0,0,0)
  PerimeterLength = 0
  Placement = pos=(2634.93,2400.2,2500) rot=(1,0,0;1.5708rad)
  PredefinedType = 0
  Profile = IPE200
  ToolOffsetFirst = 0
  ToolOffsetLast = 0
  VerticalArea = 1.94065e+06
  Width = 100
FEATURE [Part::FeaturePython] Wall002  label="NorthWall"  # Arch/BIM 166 (typed FeaturePython)
  Align = 2
  Area = 0
  Base = -> Rectangle003
  BlockHeight = 0
  BlockLength = 0
  CountBroken = 0
  CountEntire = 0
  Face = 0
  Height = 2900
  HorizontalArea = 3320000
  IfcData = attributes={"GlobalId": {"name": "GlobalId", "type": "IfcGloballyUniqueId", "is_enum": false, "enum_values": []}, "Description": {"... (+533 chars omitted),+1 more (map truncated)
  IfcType = 166
  Joint = 0
  Length = 0
  MakeBlocks = false
  MoveBase = false
  MoveWithHost = false
  Normal = (0,0,0)
  OffsetFirst = 0
  OffsetSecond = 0
  PerimeterLength = 17400
  PredefinedType = 0
  VerticalArea = 50460000
  Width = 200
FEATURE [Part::FeaturePython] Wall003  label="Wall"  # Arch/BIM 166 (typed FeaturePython)
  Align = 2
  Area = 0
  Base = -> Rectangle009
  BlockHeight = 0
  BlockLength = 0
  CountBroken = 0
  CountEntire = 0
  Face = 0
  Height = 3000
  HorizontalArea = 900000
  IfcData = attributes={"GlobalId": {"name": "GlobalId", "type": "IfcGloballyUniqueId", "is_enum": false, "enum_values": []}, "Description": {"... (+533 chars omitted),+1 more (map truncated)
  IfcType = 166
  Joint = 0
  Length = 0
  MakeBlocks = false
  MoveBase = false
  MoveWithHost = false
  Normal = (0,0,0)
  OffsetFirst = 0
  OffsetSecond = 0
  PerimeterLength = 6600
  Placement = pos=(0,0,-500) rot=(0,0,1;0rad)
  PredefinedType = 0
  VerticalArea = 19800000
  Width = 200
FEATURE [Part::Part2DObjectPython] IPE200001  # Draft 2D object (typed FeaturePython)
  FlangeThickness = 8.5
  Height = 200
  WebThickness = 5.6
  Width = 100
FEATURE [Part::FeaturePython] Structure  label="Beam5"  # Arch/BIM 24 (typed FeaturePython)
  Base = -> IPE200001
  BaseMirror = false
  BaseOffsetX = 0
  BaseOffsetY = 0
  BasePerpendicularToTool = false
  BaseRotation = 0
  ComputedLength = 1970
  FaceMaker = 0
  Height = 1970
  HorizontalArea = 382968
  IfcData = attributes={"GlobalId": {"name": "GlobalId", "type": "IfcGloballyUniqueId", "is_enum": false, "enum_values": []}, "Description": {"... (+438 chars omitted),+1 more (map truncated)
  IfcType = 24
  Length = 200
  MoveBase = false
  MoveWithHost = false
  Nodes = (2) [(0,-1.95917e-14,0),(0,-1.95917e-14,1970)]
  NodesOffset = 0
  Normal = (0,0,0)
  PerimeterLength = 0
  Placement = pos=(-5340,30,2500) rot=(0.57735,0.57735,0.57735;2.0944rad)
  PredefinedType = 0
  Profile = IPE200
  ToolOffsetFirst = 0
  ToolOffsetLast = 0
  VerticalArea = 793450
  Width = 100
FEATURE [Part::Part2DObjectPython] IPE200002  # Draft 2D object (typed FeaturePython)
  FlangeThickness = 8.5
  Height = 200
  WebThickness = 5.6
  Width = 100
FEATURE [Part::FeaturePython] Structure030  label="Beam6"  # Arch/BIM 24 (typed FeaturePython)
  Base = -> IPE200002
  BaseMirror = false
  BaseOffsetX = 0
  BaseOffsetY = 0
  BasePerpendicularToTool = false
  BaseRotation = 0
  ComputedLength = 2700
  FaceMaker = 0
  Height = 2700
  HorizontalArea = 524880
  IfcData = attributes={"GlobalId": {"name": "GlobalId", "type": "IfcGloballyUniqueId", "is_enum": false, "enum_values": []}, "Description": {"... (+438 chars omitted),+1 more (map truncated)
  IfcType = 24
  Length = 200
  MoveBase = false
  MoveWithHost = false
  Nodes = (2) [(0,-1.95917e-14,0),(0,-1.95917e-14,2700)]
  NodesOffset = 0
  Normal = (0,0,0)
  PerimeterLength = 0
  Placement = pos=(5340,30,2500) rot=(0.57735,-0.57735,-0.57735;2.0944rad)
  PredefinedType = 0
  Profile = IPE200
  ToolOffsetFirst = 0
  ToolOffsetLast = 0
  VerticalArea = 1.08545e+06
  Width = 100
FEATURE [Part::Part2DObjectPython] Rectangle  label="Base"  # Draft 2D object (typed FeaturePython)
  Area = 57200000
  ChamferSize = 0
  Columns = 1
  FilletRadius = 0
  Height = 5200
  Length = 11000
  MakeFace = true
  Placement = pos=(-5500,-2600,0) rot=(0,0,1;0rad)
  Rows = 1
  expr: .Placement.Base.x = -Spreadsheet.BaseLength / 2
  expr: .Placement.Base.y = -Spreadsheet.BaseHeight / 2
  expr: Height = Spreadsheet.BaseHeight
  expr: Length = Spreadsheet.BaseLength
FEATURE [Part::Part2DObjectPython] IPE120004  # Draft 2D object (typed FeaturePython)
  FlangeThickness = 6.3
  Height = 120
  WebThickness = 4.4
  Width = 64
FEATURE [Part::FeaturePython] Structure005  label="Col4"  # Arch/BIM 7 (typed FeaturePython)
  Base = -> IPE120004
  BaseMirror = false
  BaseOffsetX = 0
  BaseOffsetY = 0
  BasePerpendicularToTool = false
  BaseRotation = 0
  ComputedLength = 6000
  FaceMaker = 0
  Height = 6000
  HorizontalArea = 1278.96
  IfcData = attributes={"GlobalId": {"name": "GlobalId", "type": "IfcGloballyUniqueId", "is_enum": false, "enum_values": []}, "Description": {"... (+475 chars omitted),+1 more (map truncated)
  IfcType = 7
  Length = 120
  MoveBase = false
  MoveWithHost = false
  Nodes = (2) [(0,-1.61713e-15,0),(0,-1.61713e-15,6000)]
  NodesOffset = 0
  Normal = (0,0,0)
  PerimeterLength = 487.2
  Placement = pos=(-2368,2460,-1000) rot=(0,0,1;0rad)
  PredefinedType = 0
  Profile = IPE120
  ToolOffsetFirst = 0
  ToolOffsetLast = 0
  VerticalArea = 2923200
  Width = 64
  expr: .Placement.Base.x = Spreadsheet.col1xposIPE + 3000 mm
  expr: .Placement.Base.y = Spreadsheet.col1yposIPE
  expr: Height = Spreadsheet.ColHeight
FEATURE [Part::Part2DObjectPython] IPE120027  label="IPE2003"  # Draft 2D object (typed FeaturePython)
  FlangeThickness = 8.5
  Height = 200
  WebThickness = 5.6
  Width = 100
FEATURE [Part::FeaturePython] Structure027  label="Beam3-IPE200"  # Arch/BIM 7 (typed FeaturePython)
  Base = -> IPE120027
  BaseMirror = false
  BaseOffsetX = 0
  BaseOffsetY = 0
  BasePerpendicularToTool = false
  BaseRotation = 0
  ComputedLength = 4838
  FaceMaker = 0
  Height = 4838
  HorizontalArea = 940507
  IfcData = attributes={"GlobalId": {"name": "GlobalId", "type": "IfcGloballyUniqueId", "is_enum": false, "enum_values": []}, "Description": {"... (+475 chars omitted),+1 more (map truncated)
  IfcType = 7
  Length = 200
  MoveBase = false
  MoveWithHost = false
  Nodes = (2) [(0,-1.95917e-14,0),(0,-1.95917e-14,4838)]
  NodesOffset = 0
  Normal = (0,0,0)
  PerimeterLength = 0
  Placement = pos=(633.19,2400,2500) rot=(1,0,0;1.5708rad)
  PredefinedType = 0
  Profile = IPE200
  ToolOffsetFirst = 0
  ToolOffsetLast = 0
  VerticalArea = 1.94065e+06
  Width = 100
FEATURE [Part::Part2DObjectPython] IPE120003  # Draft 2D object (typed FeaturePython)
  FlangeThickness = 6.3
  Height = 120
  WebThickness = 4.4
  Width = 64
FEATURE [Part::FeaturePython] Structure004  label="Col3"  # Arch/BIM 7 (typed FeaturePython)
  Base = -> IPE120003
  BaseMirror = false
  BaseOffsetX = 0
  BaseOffsetY = 0
  BasePerpendicularToTool = false
  BaseRotation = 0
  ComputedLength = 6000
  FaceMaker = 0
  Height = 6000
  HorizontalArea = 1278.96
  IfcData = attributes={"GlobalId": {"name": "GlobalId", "type": "IfcGloballyUniqueId", "is_enum": false, "enum_values": []}, "Description": {"... (+475 chars omitted),+1 more (map truncated)
  IfcType = 7
  Length = 120
  MoveBase = false
  MoveWithHost = false
  Nodes = (2) [(0,-1.61713e-15,0),(0,-1.61713e-15,6000)]
  NodesOffset = 0
  Normal = (0,0,0)
  PerimeterLength = 487.2
  Placement = pos=(-3368,2460,-1000) rot=(0,0,1;0rad)
  PredefinedType = 0
  Profile = IPE120
  ToolOffsetFirst = 0
  ToolOffsetLast = 0
  VerticalArea = 2923200
  Width = 64
  expr: .Placement.Base.x = Spreadsheet.col1xposIPE + 2000 mm
  expr: .Placement.Base.y = Spreadsheet.col1yposIPE
  expr: Height = Spreadsheet.ColHeight
FEATURE [Part::Part2DObjectPython] IPE120002  # Draft 2D object (typed FeaturePython)
  FlangeThickness = 6.3
  Height = 120
  WebThickness = 4.4
  Width = 64
FEATURE [Part::FeaturePython] Structure003  label="Col2"  # Arch/BIM 7 (typed FeaturePython)
  Base = -> IPE120002
  BaseMirror = false
  BaseOffsetX = 0
  BaseOffsetY = 0
  BasePerpendicularToTool = false
  BaseRotation = 0
  ComputedLength = 6000
  FaceMaker = 0
  Height = 6000
  HorizontalArea = 1278.96
  IfcData = attributes={"GlobalId": {"name": "GlobalId", "type": "IfcGloballyUniqueId", "is_enum": false, "enum_values": []}, "Description": {"... (+475 chars omitted),+1 more (map truncated)
  IfcType = 7
  Length = 120
  MoveBase = false
  MoveWithHost = false
  Nodes = (2) [(0,-1.61713e-15,0),(0,-1.61713e-15,6000)]
  NodesOffset = 0
  Normal = (0,0,0)
  PerimeterLength = 487.2
  Placement = pos=(-4368,2460,-1000) rot=(0,0,1;0rad)
  PredefinedType = 0
  Profile = IPE120
  ToolOffsetFirst = 0
  ToolOffsetLast = 0
  VerticalArea = 2923200
  Width = 64
  expr: .Placement.Base.x = Spreadsheet.col1xposIPE + 1000 mm
  expr: .Placement.Base.y = Spreadsheet.col1yposIPE
  expr: Height = Spreadsheet.ColHeight
FEATURE [Part::Part2DObjectPython] IPE200  # Draft 2D object (typed FeaturePython)
  FlangeThickness = 8.5
  Height = 200
  WebThickness = 5.6
  Width = 100
FEATURE [Part::FeaturePython] Structure002  label="Beam1-IPE200"  # Arch/BIM 7 (typed FeaturePython)
  Base = -> IPE200
  BaseMirror = false
  BaseOffsetX = 0
  BaseOffsetY = 0
  BasePerpendicularToTool = false
  BaseRotation = 0
  ComputedLength = 4838
  FaceMaker = 0
  Height = 4838
  HorizontalArea = 940507
  IfcData = attributes={"GlobalId": {"name": "GlobalId", "type": "IfcGloballyUniqueId", "is_enum": false, "enum_values": []}, "Description": {"... (+475 chars omitted),+1 more (map truncated)
  IfcType = 7
  Length = 200
  MoveBase = false
  MoveWithHost = false
  Nodes = (2) [(0,-1.95917e-14,0),(0,-1.95917e-14,4838)]
  NodesOffset = 0
  Normal = (0,0,0)
  PerimeterLength = 0
  Placement = pos=(-3367.32,2400,2500) rot=(1,0,0;1.5708rad)
  PredefinedType = 0
  Profile = IPE200
  ToolOffsetFirst = 0
  ToolOffsetLast = 0
  VerticalArea = 1.94065e+06
  Width = 100
FEATURE [Part::Part2DObjectPython] IPE200004  # Draft 2D object (typed FeaturePython)
  FlangeThickness = 8.5
  Height = 200
  WebThickness = 5.6
  Width = 100
FEATURE [Part::FeaturePython] Structure031  label="Beam7"  # Arch/BIM 24 (typed FeaturePython)
  Base = -> IPE200004
  BaseMirror = false
  BaseOffsetX = 0
  BaseOffsetY = 0
  BasePerpendicularToTool = false
  BaseRotation = 0
  ComputedLength = 2000
  FaceMaker = 0
  Height = 1000
  HorizontalArea = 388800
  IfcData = attributes={"GlobalId": {"name": "GlobalId", "type": "IfcGloballyUniqueId", "is_enum": false, "enum_values": []}, "Description": {"... (+438 chars omitted),+1 more (map truncated)
  IfcType = 24
  Length = 2000
  MoveBase = false
  MoveWithHost = false
  Nodes = (2) [(0,-1.95917e-14,0),(0,-1.95917e-14,2000)]
  NodesOffset = 0
  Normal = (0,0,0)
  PerimeterLength = 0
  Placement = pos=(-3364.52,30,2500) rot=(0.57735,0.57735,0.57735;2.0944rad)
  PredefinedType = 0
  Profile = IPE200
  ToolOffsetFirst = 0
  ToolOffsetLast = 0
  VerticalArea = 805450
  Width = 100
FEATURE [App::DocumentObjectGroup] Group012  label="Beams"
  Group = -> [Structure027,Structure028,Structure029,Structure002,Structure,Structure030,Structure031]
FEATURE [Part::Part2DObjectPython] IPE200005  # Draft 2D object (typed FeaturePython)
  FlangeThickness = 8.5
  Height = 200
  WebThickness = 5.6
  Width = 100
FEATURE [Part::FeaturePython] Structure032  label="Beam8"  # Arch/BIM 24 (typed FeaturePython)
  Base = -> IPE200005
  BaseMirror = false
  BaseOffsetX = 0
  BaseOffsetY = 0
  BasePerpendicularToTool = false
  BaseRotation = 0
  ComputedLength = 1990
  FaceMaker = 0
  Height = 1990
  HorizontalArea = 386856
  IfcData = attributes={"GlobalId": {"name": "GlobalId", "type": "IfcGloballyUniqueId", "is_enum": false, "enum_values": []}, "Description": {"... (+438 chars omitted),+1 more (map truncated)
  IfcType = 24
  Length = 200
  MoveBase = false
  MoveWithHost = false
  Nodes = (2) [(0,-1.95917e-14,0),(0,-1.95917e-14,1990)]
  NodesOffset = 0
  Normal = (0,0,0)
  PerimeterLength = 0
  Placement = pos=(-1359.02,30,2500) rot=(0.57735,0.57735,0.57735;2.0944rad)
  PredefinedType = 0
  Profile = IPE200
  ToolOffsetFirst = 0
  ToolOffsetLast = 0
  VerticalArea = 801450
  Width = 100
FEATURE [Part::Part2DObjectPython] IPE200006  # Draft 2D object (typed FeaturePython)
  FlangeThickness = 8.5
  Height = 200
  WebThickness = 5.6
  Width = 100
FEATURE [Part::FeaturePython] Structure033  label="Beam9"  # Arch/BIM 24 (typed FeaturePython)
  Base = -> IPE200006
  BaseMirror = false
  BaseOffsetX = 0
  BaseOffsetY = 0
  BasePerpendicularToTool = false
  BaseRotation = 0
  ComputedLength = 1980
  FaceMaker = 0
  Height = 1980
  HorizontalArea = 384912
  IfcData = attributes={"GlobalId": {"name": "GlobalId", "type": "IfcGloballyUniqueId", "is_enum": false, "enum_values": []}, "Description": {"... (+438 chars omitted),+1 more (map truncated)
  IfcType = 24
  Length = 200
  MoveBase = false
  MoveWithHost = false
  Nodes = (2) [(0,-1.95917e-14,0),(0,-1.95917e-14,1980)]
  NodesOffset = 0
  Normal = (0,0,0)
  PerimeterLength = 0
  Placement = pos=(635.99,30,2507.58) rot=(0.57735,0.57735,0.57735;2.0944rad)
  PredefinedType = 0
  Profile = IPE200
  ToolOffsetFirst = 0
  ToolOffsetLast = 0
  VerticalArea = 797450
  Width = 100
FEATURE [Part::Part2DObjectPython] IPE200008  # Draft 2D object (typed FeaturePython)
  FlangeThickness = 8.5
  Height = 200
  WebThickness = 5.6
  Width = 100
FEATURE [Part::FeaturePython] Structure034  label="Beam10"  # Arch/BIM 24 (typed FeaturePython)
  Base = -> IPE200008
  BaseMirror = false
  BaseOffsetX = 0
  BaseOffsetY = 0
  BasePerpendicularToTool = false
  BaseRotation = 0
  ComputedLength = 2705
  FaceMaker = 0
  Height = 2705
  HorizontalArea = 525852
  IfcData = attributes={"GlobalId": {"name": "GlobalId", "type": "IfcGloballyUniqueId", "is_enum": false, "enum_values": []}, "Description": {"... (+438 chars omitted),+1 more (map truncated)
  IfcType = 24
  Length = 200
  MoveBase = false
  MoveWithHost = false
  Nodes = (2) [(0,-1.95917e-14,0),(0,-1.95917e-14,2705)]
  NodesOffset = 0
  Normal = (0,0,0)
  PerimeterLength = 0
  Placement = pos=(2636.96,2460.25,2500) rot=(0.57735,0.57735,0.57735;2.0944rad)
  PredefinedType = 0
  Profile = IPE200
  ToolOffsetFirst = 0
  ToolOffsetLast = 0
  VerticalArea = 1.08745e+06
  Width = 100
FEATURE [Part::Part2DObjectPython] IPE200009  # Draft 2D object (typed FeaturePython)
  FlangeThickness = 8.5
  Height = 200
  WebThickness = 5.6
  Width = 100
FEATURE [Part::FeaturePython] Structure035  label="Beam11"  # Arch/BIM 24 (typed FeaturePython)
  Base = -> IPE200009
  BaseMirror = false
  BaseOffsetX = 0
  BaseOffsetY = 0
  BasePerpendicularToTool = false
  BaseRotation = 0
  ComputedLength = 2997
  FaceMaker = 0
  Height = 2997
  HorizontalArea = 582617
  IfcData = attributes={"GlobalId": {"name": "GlobalId", "type": "IfcGloballyUniqueId", "is_enum": false, "enum_values": []}, "Description": {"... (+438 chars omitted),+1 more (map truncated)
  IfcType = 24
  Length = 200
  MoveBase = false
  MoveWithHost = false
  Nodes = (2) [(0,-1.95917e-14,0),(0,-1.95917e-14,2997)]
  NodesOffset = 0
  Normal = (0,0,0)
  PerimeterLength = 0
  Placement = pos=(3540,5430,2800) rot=(1,0,0;1.5708rad)
  PredefinedType = 0
  Profile = IPE200
  ToolOffsetFirst = 0
  ToolOffsetLast = 0
  VerticalArea = 1.20425e+06
  Width = 100
FEATURE [Part::Part2DObjectPython] IPE200010  # Draft 2D object (typed FeaturePython)
  FlangeThickness = 8.5
  Height = 200
  WebThickness = 5.6
  Width = 100
FEATURE [Part::FeaturePython] Structure036  label="Beam12"  # Arch/BIM 24 (typed FeaturePython)
  Base = -> IPE200010
  BaseMirror = false
  BaseOffsetX = 0
  BaseOffsetY = 0
  BasePerpendicularToTool = false
  BaseRotation = 0
  ComputedLength = 2997
  FaceMaker = 0
  Height = 2997
  HorizontalArea = 582617
  IfcData = attributes={"GlobalId": {"name": "GlobalId", "type": "IfcGloballyUniqueId", "is_enum": false, "enum_values": []}, "Description": {"... (+438 chars omitted),+1 more (map truncated)
  IfcType = 24
  Length = 200
  MoveBase = false
  MoveWithHost = false
  Nodes = (2) [(0,-1.95917e-14,0),(0,-1.95917e-14,2997)]
  NodesOffset = 0
  Normal = (0,0,0)
  PerimeterLength = 0
  Placement = pos=(4544.78,5428.53,2800) rot=(1,0,0;1.5708rad)
  PredefinedType = 0
  Profile = IPE200
  ToolOffsetFirst = 0
  ToolOffsetLast = 0
  VerticalArea = 1.20425e+06
  Width = 100
FEATURE [Part::Part2DObjectPython] IPE120  # Draft 2D object (typed FeaturePython)
  FlangeThickness = 6.3
  Height = 120
  WebThickness = 4.4
  Width = 64
FEATURE [Part::FeaturePython] Structure037  label="Col41"  # Arch/BIM 24 (typed FeaturePython)
  Base = -> IPE120
  BaseMirror = false
  BaseOffsetX = 0
  BaseOffsetY = 0
  BasePerpendicularToTool = false
  BaseRotation = 0
  ComputedLength = 120
  FaceMaker = 0
  Height = 120
  HorizontalArea = 1278.96
  IfcData = attributes={"GlobalId": {"name": "GlobalId", "type": "IfcGloballyUniqueId", "is_enum": false, "enum_values": []}, "Description": {"... (+438 chars omitted),+1 more (map truncated)
  IfcType = 24
  Length = 120
  MoveBase = false
  MoveWithHost = false
  Nodes = (2) [(0,-1.61713e-15,0),(0,-1.61713e-15,120)]
  NodesOffset = 0
  Normal = (0,0,0)
  PerimeterLength = 487.2
  Placement = pos=(3540,2464.41,2600) rot=(0,0,1;1.5708rad)
  PredefinedType = 0
  Profile = IPE120
  ToolOffsetFirst = 0
  ToolOffsetLast = 0
  VerticalArea = 58464
  Width = 64
FEATURE [Part::Part2DObjectPython] IPE200011  # Draft 2D object (typed FeaturePython)
  FlangeThickness = 6.3
  Height = 120
  WebThickness = 4.4
  Width = 64
FEATURE [Part::FeaturePython] Structure038  label="Col42"  # Arch/BIM 24 (typed FeaturePython)
  Base = -> IPE200011
  BaseMirror = false
  BaseOffsetX = 0
  BaseOffsetY = 0
  BasePerpendicularToTool = false
  BaseRotation = 0
  ComputedLength = 120
  FaceMaker = 0
  Height = 100
  HorizontalArea = 1278.96
  IfcData = attributes={"GlobalId": {"name": "GlobalId", "type": "IfcGloballyUniqueId", "is_enum": false, "enum_values": []}, "Description": {"... (+438 chars omitted),+1 more (map truncated)
  IfcType = 24
  Length = 120
  MoveBase = false
  MoveWithHost = false
  Nodes = (2) [(0,-1.61713e-15,0),(0,-1.61713e-15,120)]
  NodesOffset = 0
  Normal = (0,0,0)
  PerimeterLength = 487.2
  Placement = pos=(4544.49,2460.09,2600) rot=(0,0,1;1.5708rad)
  PredefinedType = 0
  Profile = IPE120
  ToolOffsetFirst = 0
  ToolOffsetLast = 0
  VerticalArea = 58464
  Width = 64
FEATURE [App::DocumentObjectGroup] Group006  label="ColsLaundry"
  Group = -> [Structure018,Structure011,Structure013,Structure014,Structure017,Structure016,Structure015,Structure012,Structure038,Structure037]
FEATURE [App::DocumentObjectGroup] Group005  label="Laundry"
  Group = -> [Group004,Group006]
FEATURE [Part::Part2DObjectPython] IPE200012  # Draft 2D object (typed FeaturePython)
  FlangeThickness = 6.3
  Height = 120
  WebThickness = 4.4
  Width = 64
FEATURE [Part::FeaturePython] Structure039  label="Col01"  # Arch/BIM 24 (typed FeaturePython)
  Base = -> IPE200012
  BaseMirror = false
  BaseOffsetX = 0
  BaseOffsetY = 0
  BasePerpendicularToTool = false
  BaseRotation = 0
  ComputedLength = 6000
  FaceMaker = 0
  Height = 6000
  HorizontalArea = 1278.96
  IfcData = attributes={"GlobalId": {"name": "GlobalId", "type": "IfcGloballyUniqueId", "is_enum": false, "enum_values": []}, "Description": {"... (+438 chars omitted),+1 more (map truncated)
  IfcType = 24
  Length = 120
  MoveBase = false
  MoveWithHost = false
  Nodes = (2) [(0,-1.61713e-15,0),(0,-1.61713e-15,6000)]
  NodesOffset = 0
  Normal = (0,0,0)
  PerimeterLength = 487.2
  Placement = pos=(-5368.01,2460,-1000) rot=(0,0,1;0rad)
  PredefinedType = 0
  Profile = IPE120
  ToolOffsetFirst = 0
  ToolOffsetLast = 0
  VerticalArea = 2923200
  Width = 64
FEATURE [App::DocumentObjectGroup] Group003  label="ColsN"
  Group = -> [Structure003,Structure004,Structure005,Structure006,Structure007,Structure008,Structure009,Structure010,Structure039]
FEATURE [App::DocumentObjectGroup] Group007  label="North"
  Group = -> [Group001,Group003]
FEATURE [Part::Part2DObjectPython] IPE200013  # Draft 2D object (typed FeaturePython)
  FlangeThickness = 6.3
  Height = 120
  WebThickness = 4.4
  Width = 64
FEATURE [Part::FeaturePython] Structure040  label="Beam13"  # Arch/BIM 24 (typed FeaturePython)
  Base = -> IPE200013
  BaseMirror = false
  BaseOffsetX = 0
  BaseOffsetY = 0
  BasePerpendicularToTool = false
  BaseRotation = 0
  ComputedLength = 2630
  FaceMaker = 0
  Height = 2630
  HorizontalArea = 325068
  IfcData = attributes={"GlobalId": {"name": "GlobalId", "type": "IfcGloballyUniqueId", "is_enum": false, "enum_values": []}, "Description": {"... (+438 chars omitted),+1 more (map truncated)
  IfcType = 24
  Length = 120
  MoveBase = false
  MoveWithHost = false
  Nodes = (2) [(0,-1.61713e-15,0),(0,-1.61713e-15,2630)]
  NodesOffset = 0
  Normal = (0,0,0)
  PerimeterLength = 0
  Placement = pos=(2719,4432,2800) rot=(0.57735,0.57735,0.57735;2.0944rad)
  PredefinedType = 0
  Profile = IPE120
  ToolOffsetFirst = 0
  ToolOffsetLast = 0
  VerticalArea = 633758
  Width = 64
FEATURE [Part::Part2DObjectPython] IPE200014  # Draft 2D object (typed FeaturePython)
  FlangeThickness = 6.3
  Height = 120
  WebThickness = 4.4
  Width = 64
FEATURE [Part::FeaturePython] Structure041  label="Column001"  # Arch/BIM 24 (typed FeaturePython)
  Base = -> IPE200014
  BaseMirror = false
  BaseOffsetX = 0
  BaseOffsetY = 0
  BasePerpendicularToTool = false
  BaseRotation = 0
  ComputedLength = 2630
  FaceMaker = 0
  Height = 2630
  HorizontalArea = 325068
  IfcData = attributes={"GlobalId": {"name": "GlobalId", "type": "IfcGloballyUniqueId", "is_enum": false, "enum_values": []}, "Description": {"... (+438 chars omitted),+1 more (map truncated)
  IfcType = 24
  Length = 120
  MoveBase = false
  MoveWithHost = false
  Nodes = (2) [(0,-1.61713e-15,0),(0,-1.61713e-15,2630)]
  NodesOffset = 0
  Normal = (0,0,0)
  PerimeterLength = 0
  Placement = pos=(2720,3432,2800) rot=(0.57735,0.57735,0.57735;2.0944rad)
  PredefinedType = 0
  Profile = IPE120
  ToolOffsetFirst = 0
  ToolOffsetLast = 0
  VerticalArea = 633758
  Width = 64
FEATURE [Part::Part2DObjectPython] IPE200015  # Draft 2D object (typed FeaturePython)
  FlangeThickness = 6.3
  Height = 120
  WebThickness = 4.4
  Width = 64
FEATURE [Part::FeaturePython] Structure042  label="Col20"  # Arch/BIM 24 (typed FeaturePython)
  Base = -> IPE200015
  BaseMirror = false
  BaseOffsetX = 0
  BaseOffsetY = 0
  BasePerpendicularToTool = false
  BaseRotation = 0
  ComputedLength = 6000
  FaceMaker = 0
  Height = 6000
  HorizontalArea = 1278.96
  IfcData = attributes={"GlobalId": {"name": "GlobalId", "type": "IfcGloballyUniqueId", "is_enum": false, "enum_values": []}, "Description": {"... (+438 chars omitted),+1 more (map truncated)
  IfcType = 24
  Length = 120
  MoveBase = false
  MoveWithHost = false
  Nodes = (2) [(0,-1.61713e-15,0),(0,-1.61713e-15,6000)]
  NodesOffset = 0
  Normal = (0,0,0)
  PerimeterLength = 487.2
  Placement = pos=(5400.05,-2500.3,-1000) rot=(0,0,1;1.5708rad)
  PredefinedType = 0
  Profile = IPE120
  ToolOffsetFirst = 0
  ToolOffsetLast = 0
  VerticalArea = 2923200
  Width = 64
FEATURE [App::DocumentObjectGroup] Group010  label="ColE"
  Group = -> [Structure024,Structure042]
FEATURE [App::DocumentObjectGroup] Group009  label="East"
  Group = -> [Group010,Group011]
FEATURE [App::DocumentObjectGroup] Group  label="Columns"
  Group = -> [Group002,Group005,Group007,Group009]
FEATURE [Part::Part2DObjectPython] IPE200016  # Draft 2D object (typed FeaturePython)
  FlangeThickness = 6.3
  Height = 120
  WebThickness = 4.4
  Width = 64
FEATURE [Part::FeaturePython] Structure043  label="Beam8-IPE120"  # Arch/BIM 24 (typed FeaturePython)
  Base = -> IPE200016
  BaseMirror = false
  BaseOffsetX = 0
  BaseOffsetY = 0
  BasePerpendicularToTool = false
  BaseRotation = 0
  ComputedLength = 8000
  FaceMaker = 0
  Height = 8000
  HorizontalArea = 988800
  IfcData = attributes={"GlobalId": {"name": "GlobalId", "type": "IfcGloballyUniqueId", "is_enum": false, "enum_values": []}, "Description": {"... (+438 chars omitted),+1 more (map truncated)
  IfcType = 24
  Length = 120
  MoveBase = false
  MoveWithHost = false
  Nodes = (2) [(0,-1.61713e-15,0),(0,-1.61713e-15,8000)]
  NodesOffset = 0
  Normal = (0,0,0)
  PerimeterLength = 0
  Placement = pos=(-5365.81,2460,2540) rot=(0.58,0.58,0.58;2.0944rad)
  PredefinedType = 0
  Profile = IPE120
  ToolOffsetFirst = 0
  ToolOffsetLast = 0
  VerticalArea = 1.92256e+06
  Width = 64
FEATURE [Part::Part2DObjectPython] IPE200017  # Draft 2D object (typed FeaturePython)
  FlangeThickness = 6.3
  Height = 120
  WebThickness = 4.4
  Width = 64
FEATURE [Part::FeaturePython] Structure044  label="Beam9-IPE120"  # Arch/BIM 24 (typed FeaturePython)
  Base = -> IPE200017
  BaseMirror = false
  BaseOffsetX = 0
  BaseOffsetY = 0
  BasePerpendicularToTool = false
  BaseRotation = 0
  ComputedLength = 10710
  FaceMaker = 0
  Height = 10710
  HorizontalArea = 1.32376e+06
  IfcData = attributes={"GlobalId": {"name": "GlobalId", "type": "IfcGloballyUniqueId", "is_enum": false, "enum_values": []}, "Description": {"... (+438 chars omitted),+1 more (map truncated)
  IfcType = 24
  Length = 120
  MoveBase = false
  MoveWithHost = false
  Nodes = (2) [(0,-1.61713e-15,0),(0,-1.61713e-15,10710)]
  NodesOffset = 0
  Normal = (0,0,0)
  PerimeterLength = 0
  Placement = pos=(-5365.81,-2500,2540) rot=(0.58,0.58,0.58;2.0944rad)
  PredefinedType = 0
  Profile = IPE120
  ToolOffsetFirst = 0
  ToolOffsetLast = 0
  VerticalArea = 2.57296e+06
  Width = 64
FEATURE [Part::Part2DObjectPython] IPE200018  # Draft 2D object (typed FeaturePython)
  FlangeThickness = 6.3
  Height = 120
  WebThickness = 4.4
  Width = 64
FEATURE [Part::FeaturePython] Structure045  label="Beam10-IPE120"  # Arch/BIM 24 (typed FeaturePython)
  Base = -> IPE200018
  BaseMirror = false
  BaseOffsetX = 0
  BaseOffsetY = 0
  BasePerpendicularToTool = false
  BaseRotation = 0
  ComputedLength = 2370
  FaceMaker = 0
  Height = 2370
  HorizontalArea = 292932
  IfcData = attributes={"GlobalId": {"name": "GlobalId", "type": "IfcGloballyUniqueId", "is_enum": false, "enum_values": []}, "Description": {"... (+438 chars omitted),+1 more (map truncated)
  IfcType = 24
  Length = 120
  MoveBase = false
  MoveWithHost = false
  Nodes = (2) [(0,-1.61713e-15,0),(0,-1.61713e-15,2370)]
  NodesOffset = 0
  Normal = (0,0,0)
  PerimeterLength = 0
  Placement = pos=(-5369.52,2400,2540) rot=(1,0,0;1.5708rad)
  PredefinedType = 0
  Profile = IPE120
  ToolOffsetFirst = 0
  ToolOffsetLast = 0
  VerticalArea = 571358
  Width = 64
FEATURE [Part::Part2DObjectPython] IPE200019  # Draft 2D object (typed FeaturePython)
  FlangeThickness = 6.3
  Height = 120
  WebThickness = 4.4
  Width = 64
FEATURE [Part::FeaturePython] Structure046  label="Column"  # Arch/BIM 24 (typed FeaturePython)
  Base = -> IPE200019
  BaseMirror = false
  BaseOffsetX = 0
  BaseOffsetY = 0
  BasePerpendicularToTool = false
  BaseRotation = 0
  ComputedLength = 4900
  FaceMaker = 0
  Height = 4900
  HorizontalArea = 605640
  IfcData = attributes={"GlobalId": {"name": "GlobalId", "type": "IfcGloballyUniqueId", "is_enum": false, "enum_values": []}, "Description": {"... (+438 chars omitted),+1 more (map truncated)
  IfcType = 24
  Length = 120
  MoveBase = false
  MoveWithHost = false
  Nodes = (2) [(0,-1.61713e-15,0),(0,-1.61713e-15,4900)]
  NodesOffset = 0
  Normal = (0,0,0)
  PerimeterLength = 0
  Placement = pos=(-4366.36,2400,2540) rot=(1,0,0;1.5708rad)
  PredefinedType = 0
  Profile = IPE120
  ToolOffsetFirst = 0
  ToolOffsetLast = 0
  VerticalArea = 1.17856e+06
  Width = 64
FEATURE [Part::Part2DObjectPython] IPE200020  # Draft 2D object (typed FeaturePython)
  FlangeThickness = 6.3
  Height = 120
  WebThickness = 4.4
  Width = 64
FEATURE [Part::FeaturePython] Structure047  label="Column002"  # Arch/BIM 24 (typed FeaturePython)
  Base = -> IPE200020
  BaseMirror = false
  BaseOffsetX = 0
  BaseOffsetY = 0
  BasePerpendicularToTool = false
  BaseRotation = 0
  ComputedLength = 4900
  FaceMaker = 0
  Height = 4900
  HorizontalArea = 605640
  IfcData = attributes={"GlobalId": {"name": "GlobalId", "type": "IfcGloballyUniqueId", "is_enum": false, "enum_values": []}, "Description": {"... (+438 chars omitted),+1 more (map truncated)
  IfcType = 24
  Length = 120
  MoveBase = false
  MoveWithHost = false
  Nodes = (2) [(0,-1.61713e-15,0),(0,-1.61713e-15,4900)]
  NodesOffset = 0
  Normal = (0,0,0)
  PerimeterLength = 0
  Placement = pos=(-2358.59,2400,2540) rot=(1,0,0;1.5708rad)
  PredefinedType = 0
  Profile = IPE120
  ToolOffsetFirst = 0
  ToolOffsetLast = 0
  VerticalArea = 1.17856e+06
  Width = 64
FEATURE [Part::Part2DObjectPython] IPE200021  # Draft 2D object (typed FeaturePython)
  FlangeThickness = 6.3
  Height = 120
  WebThickness = 4.4
  Width = 64
FEATURE [Part::FeaturePython] Structure048  label="Column003"  # Arch/BIM 24 (typed FeaturePython)
  Base = -> IPE200021
  BaseMirror = false
  BaseOffsetX = 0
  BaseOffsetY = 0
  BasePerpendicularToTool = false
  BaseRotation = 0
  ComputedLength = 4900
  FaceMaker = 0
  Height = 4900
  HorizontalArea = 605640
  IfcData = attributes={"GlobalId": {"name": "GlobalId", "type": "IfcGloballyUniqueId", "is_enum": false, "enum_values": []}, "Description": {"... (+438 chars omitted),+1 more (map truncated)
  IfcType = 24
  Length = 120
  MoveBase = false
  MoveWithHost = false
  Nodes = (2) [(0,-1.61713e-15,0),(0,-1.61713e-15,4900)]
  NodesOffset = 0
  Normal = (0,0,0)
  PerimeterLength = 0
  Placement = pos=(-368,2400,2540) rot=(1,0,0;1.5708rad)
  PredefinedType = 0
  Profile = IPE120
  ToolOffsetFirst = 0
  ToolOffsetLast = 0
  VerticalArea = 1.17856e+06
  Width = 64
FEATURE [Part::Part2DObjectPython] IPE200022  # Draft 2D object (typed FeaturePython)
  FlangeThickness = 6.3
  Height = 120
  WebThickness = 4.4
  Width = 64
FEATURE [Part::FeaturePython] Structure049  label="Column004"  # Arch/BIM 24 (typed FeaturePython)
  Base = -> IPE200022
  BaseMirror = false
  BaseOffsetX = 0
  BaseOffsetY = 0
  BasePerpendicularToTool = false
  BaseRotation = 0
  ComputedLength = 4900
  FaceMaker = 0
  Height = 4900
  HorizontalArea = 605640
  IfcData = attributes={"GlobalId": {"name": "GlobalId", "type": "IfcGloballyUniqueId", "is_enum": false, "enum_values": []}, "Description": {"... (+438 chars omitted),+1 more (map truncated)
  IfcType = 24
  Length = 120
  MoveBase = false
  MoveWithHost = false
  Nodes = (2) [(0,-1.61713e-15,0),(0,-1.61713e-15,4900)]
  NodesOffset = 0
  Normal = (0,0,0)
  PerimeterLength = 0
  Placement = pos=(1632.59,2400,2540) rot=(1,0,0;1.5708rad)
  PredefinedType = 0
  Profile = IPE120
  ToolOffsetFirst = 0
  ToolOffsetLast = 0
  VerticalArea = 1.17856e+06
  Width = 64
FEATURE [Part::Part2DObjectPython] IPE200023  # Draft 2D object (typed FeaturePython)
  FlangeThickness = 6.3
  Height = 120
  WebThickness = 4.4
  Width = 64
FEATURE [Part::FeaturePython] Structure050  label="Column005"  # Arch/BIM 24 (typed FeaturePython)
  Base = -> IPE200023
  BaseMirror = false
  BaseOffsetX = 0
  BaseOffsetY = 0
  BasePerpendicularToTool = false
  BaseRotation = 0
  ComputedLength = 9710
  FaceMaker = 0
  Height = 9710
  HorizontalArea = 1.20016e+06
  IfcData = attributes={"GlobalId": {"name": "GlobalId", "type": "IfcGloballyUniqueId", "is_enum": false, "enum_values": []}, "Description": {"... (+438 chars omitted),+1 more (map truncated)
  IfcType = 24
  Length = 120
  MoveBase = false
  MoveWithHost = false
  Nodes = (2) [(0,-1.61713e-15,0),(0,-1.61713e-15,9710)]
  NodesOffset = 0
  Normal = (0,0,0)
  PerimeterLength = 0
  Placement = pos=(-4364.16,-700,2540) rot=(0.58,0.58,0.58;2.0944rad)
  PredefinedType = 0
  Profile = IPE120
  ToolOffsetFirst = 0
  ToolOffsetLast = 0
  VerticalArea = 2.33296e+06
  Width = 64
FEATURE [Part::Part2DObjectPython] IPE200024  # Draft 2D object (typed FeaturePython)
  FlangeThickness = 6.3
  Height = 120
  WebThickness = 4.4
  Width = 64
FEATURE [Part::FeaturePython] Structure051  label="Column006"  # Arch/BIM 24 (typed FeaturePython)
  Base = -> IPE200024
  BaseMirror = false
  BaseOffsetX = 0
  BaseOffsetY = 0
  BasePerpendicularToTool = false
  BaseRotation = 0
  ComputedLength = 9750
  FaceMaker = 0
  Height = 9750
  HorizontalArea = 1.2051e+06
  IfcData = attributes={"GlobalId": {"name": "GlobalId", "type": "IfcGloballyUniqueId", "is_enum": false, "enum_values": []}, "Description": {"... (+438 chars omitted),+1 more (map truncated)
  IfcType = 24
  Length = 120
  MoveBase = false
  MoveWithHost = false
  Nodes = (2) [(0,-1.61713e-15,0),(0,-1.61713e-15,9750)]
  NodesOffset = 0
  Normal = (0,0,0)
  PerimeterLength = 0
  Placement = pos=(-4364.16,-1452.21,2540) rot=(0.58,0.58,0.58;2.0944rad)
  PredefinedType = 0
  Profile = IPE120
  ToolOffsetFirst = 0
  ToolOffsetLast = 0
  VerticalArea = 2.34256e+06
  Width = 64
FEATURE [Part::Part2DObjectPython] IPE200025  # Draft 2D object (typed FeaturePython)
  FlangeThickness = 6.3
  Height = 120
  WebThickness = 4.4
  Width = 64
FEATURE [Part::FeaturePython] Structure052  label="Column007"  # Arch/BIM 24 (typed FeaturePython)
  Base = -> IPE200025
  BaseMirror = false
  BaseOffsetX = 0
  BaseOffsetY = 0
  BasePerpendicularToTool = false
  BaseRotation = 0
  ComputedLength = 4900
  FaceMaker = 0
  Height = 4900
  HorizontalArea = 605640
  IfcData = attributes={"GlobalId": {"name": "GlobalId", "type": "IfcGloballyUniqueId", "is_enum": false, "enum_values": []}, "Description": {"... (+438 chars omitted),+1 more (map truncated)
  IfcType = 24
  Length = 120
  MoveBase = false
  MoveWithHost = false
  Nodes = (2) [(0,-1.61713e-15,0),(0,-1.61713e-15,4900)]
  NodesOffset = 0
  Normal = (0,0,0)
  PerimeterLength = 0
  Placement = pos=(5402,2431.8,2532.86) rot=(1,0,0;1.5708rad)
  PredefinedType = 0
  Profile = IPE120
  ToolOffsetFirst = 0
  ToolOffsetLast = 0
  VerticalArea = 1.17856e+06
  Width = 64
